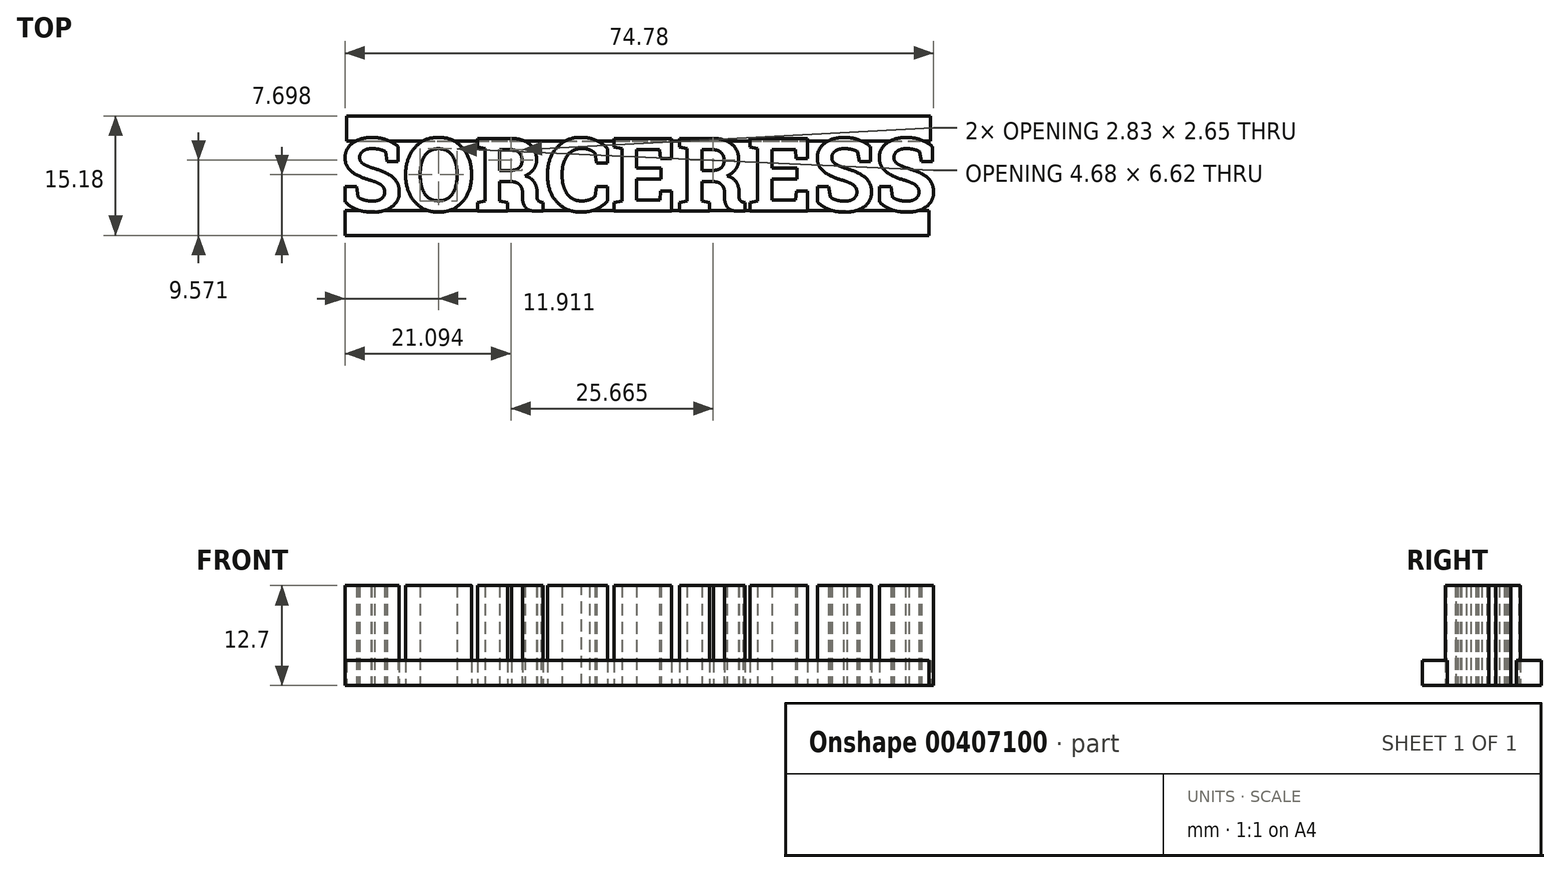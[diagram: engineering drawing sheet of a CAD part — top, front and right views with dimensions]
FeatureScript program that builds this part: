
annotation { "Feature Type Name" : "Feature", "Feature Type Description" : "" }
export const myFeature = defineFeature(function(context is Context, id is Id, definition is map)
    precondition{}
    {
        {
            var Q0;
            Q0=qCreatedBy(makeId("Top.planeOp"),FACE);
            var sketch = newSketch(context, id + "F0", { "sketchPlane" : qUnion([Q0])});
            skText(sketch, "E0", { "text": "SORCERESS", "fontName": "RobotoSlab-Bold.ttf"});
            const initialGuessF0  = {"E0": [-0.01004, -0.005, 1, 0, 0.00936]};
            skSetInitialGuess(sketch, initialGuessF0);
            skSolve(sketch);
        }
        {
            var Q0;
            Q0 = qSketchRegion(id + "F0", true);
            var Q1;
            Q1 = qSketchRegion(id + "F2", true);
            extrude(context, id + "F1", {"entities" : qUnion([Q0, Q1]), "depth" : 12.7 * mm});
        }
        {
            var Q0;
            Q0=qCreatedBy(makeId("Top.planeOp"),FACE);
            var sketch = newSketch(context, id + "F2", { "sketchPlane" : qUnion([Q0])});
            skLineSegment(sketch, "E1.bottom", {"start": v(-9.45, -8.08) * mm, "end": v(64.72, -8.08) * mm});
            skLineSegment(sketch, "E1.top", {"start": v(-9.45, -4.9) * mm, "end": v(64.72, -4.9) * mm});
            skLineSegment(sketch, "E1.left", {"start": v(-9.45, -8.08) * mm, "end": v(-9.45, -4.9) * mm});
            skLineSegment(sketch, "E1.right", {"start": v(64.72, -8.08) * mm, "end": v(64.72, -4.9) * mm});
            skSolve(sketch);
        }
        {
            var Q0;
            Q0 = qSketchRegion(id + "F2", true);
            extrude(context, id + "F3", {"entities" : qUnion([Q0]), "depth" : 3.17 * mm});
        }
        {
            var Q0;
            Q0=qCreatedBy(makeId("Top.planeOp"),FACE);
            var sketch = newSketch(context, id + "F4", { "sketchPlane" : qUnion([Q0])});
            skLineSegment(sketch, "E2.bottom", {"start": v(-9.2, 3.92) * mm, "end": v(64.96, 3.92) * mm});
            skLineSegment(sketch, "E2.top", {"start": v(-9.2, 7.1) * mm, "end": v(64.96, 7.1) * mm});
            skLineSegment(sketch, "E2.left", {"start": v(-9.2, 3.92) * mm, "end": v(-9.2, 7.1) * mm});
            skLineSegment(sketch, "E2.right", {"start": v(64.96, 3.92) * mm, "end": v(64.96, 7.1) * mm});
            skSolve(sketch);
        }
        {
            var Q0;
            Q0 = qSketchRegion(id + "F4", true);
            extrude(context, id + "F5", {"entities" : qUnion([Q0]), "depth" : 3.17 * mm});
        }
    });
